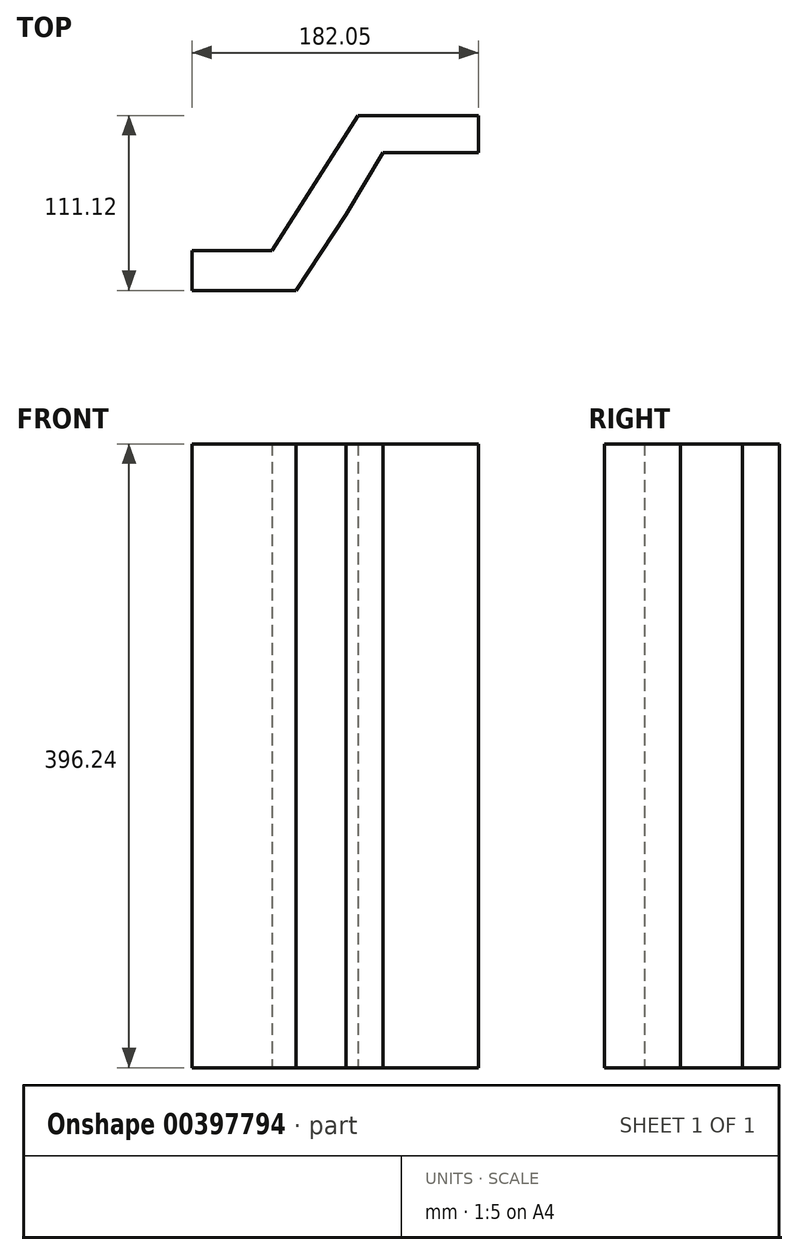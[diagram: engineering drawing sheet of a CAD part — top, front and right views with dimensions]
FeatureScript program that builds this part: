
annotation { "Feature Type Name" : "Feature", "Feature Type Description" : "" }
export const myFeature = defineFeature(function(context is Context, id is Id, definition is map)
    precondition{}
    {
        {
            var Q0;
            Q0=qCreatedBy(makeId("Top.planeOp"),FACE);
            var sketch = newSketch(context, id + "F0", { "sketchPlane" : qUnion([Q0])});
            skLineSegment(sketch, "E0", {"start": v(-0.4, 62.9) * mm, "end": v(76.3, 62.9) * mm});
            skLineSegment(sketch, "E1", {"start": v(76.3, 62.9) * mm, "end": v(76.3, 39.37) * mm});
            skLineSegment(sketch, "E2", {"start": v(76.3, 39.37) * mm, "end": v(15.5, 39.37) * mm});
            skLineSegment(sketch, "E3", {"start": v(15.5, 39.37) * mm, "end": v(-8.01, 0) * mm});
            skLineSegment(sketch, "E4", {"start": v(-0.4, 62.9) * mm, "end": v(-54.94, -22.83) * mm});
            skLineSegment(sketch, "E5", {"start": v(-54.94, -22.83) * mm, "end": v(-105.74, -22.83) * mm});
            skLineSegment(sketch, "E6", {"start": v(-105.74, -22.83) * mm, "end": v(-105.74, -48.23) * mm});
            skLineSegment(sketch, "E7", {"start": v(-105.74, -48.23) * mm, "end": v(-39.7, -48.23) * mm});
            skLineSegment(sketch, "E8", {"start": v(-39.7, -48.23) * mm, "end": v(-8.01, 0) * mm});
            skSolve(sketch);
        }
        {
            var Q0;
            Q0=makeQuery(id+"F0.imprint","IMPRINT",FACE,{"disambiguationData":[TD([[makeQuery(id+"F0.imprint","IMPRINT",EDGE,{"derivedFrom":sQuery(id+"F0.wireOp",EDGE,"E0")}),-1.0]])]});
            extrude(context, id + "F1", {"entities" : qUnion([Q0]), "depth" : 396.24 * mm});
        }
    });
